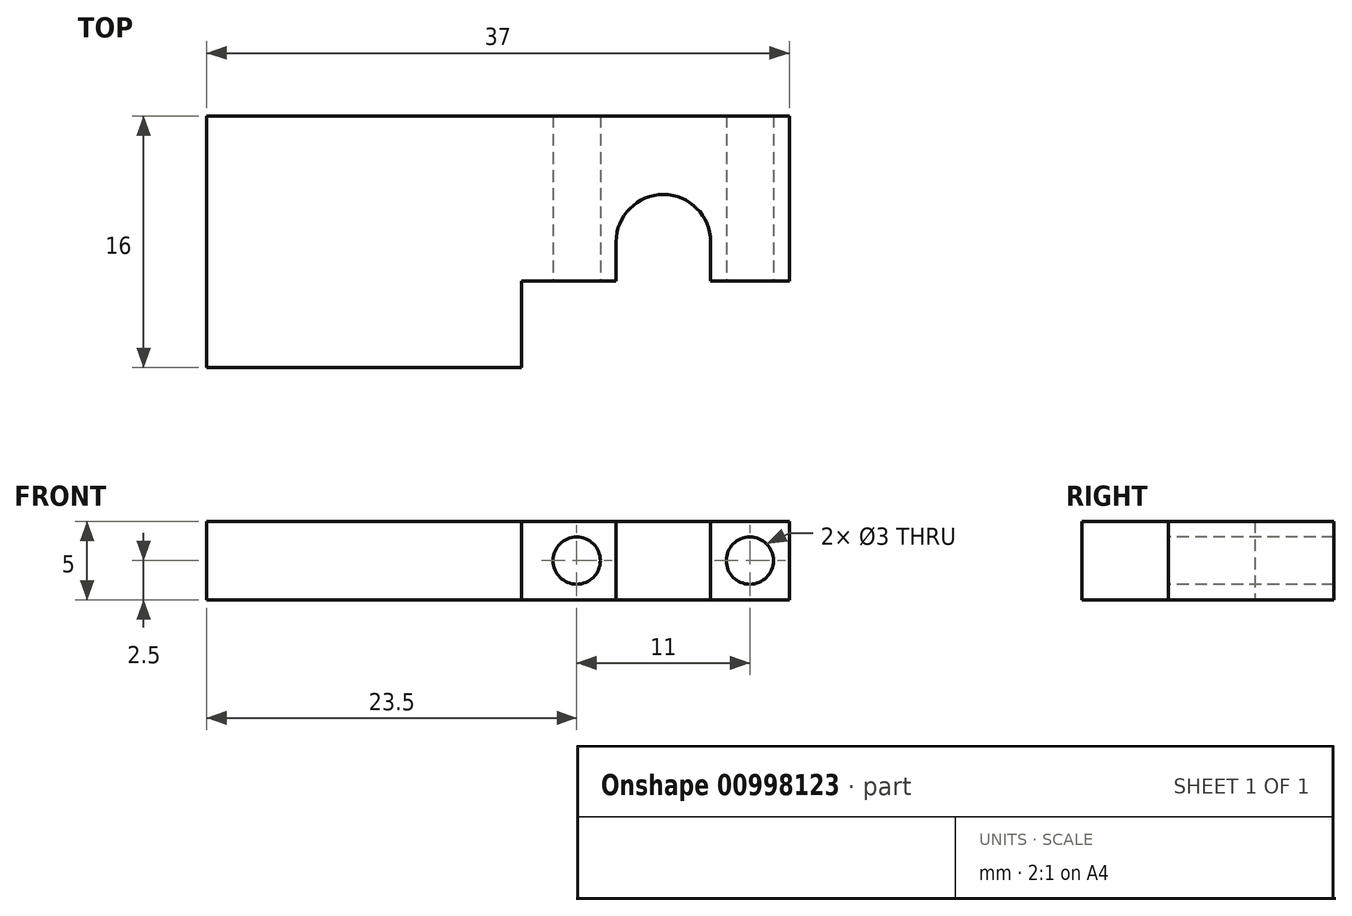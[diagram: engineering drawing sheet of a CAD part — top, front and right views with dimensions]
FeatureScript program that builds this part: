
annotation { "Feature Type Name" : "Feature", "Feature Type Description" : "" }
export const myFeature = defineFeature(function(context is Context, id is Id, definition is map)
    precondition{}
    {
        {
            var Q0;
            Q0=qCreatedBy(makeId("Top.planeOp"),FACE);
            var sketch = newSketch(context, id + "F0", { "sketchPlane" : qUnion([Q0])});
            skLineSegment(sketch, "E0", {"start": v(0, 0) * mm, "end": v(20, 0) * mm});
            skArc(sketch, "E1", {"start": v(32, 8) * mm, "mid": v(29, 11) * mm, "end": v(26, 8) * mm});
            skLineSegment(sketch, "E2", {"start": v(37, 16) * mm, "end": v(0, 16) * mm});
            skLineSegment(sketch, "E3", {"start": v(0, 16) * mm, "end": v(0, 0) * mm});
            skLineSegment(sketch, "E4", {"start": v(20, 0) * mm, "end": v(20, 5.5) * mm});
            skLineSegment(sketch, "E5", {"start": v(20, 5.5) * mm, "end": v(26, 5.5) * mm});
            skLineSegment(sketch, "E6", {"start": v(26, 5.5) * mm, "end": v(26, 8) * mm});
            skLineSegment(sketch, "E7", {"start": v(37, 5.5) * mm, "end": v(37, 16) * mm});
            skLineSegment(sketch, "E8", {"start": v(32, 8) * mm, "end": v(32, 5.5) * mm});
            skLineSegment(sketch, "E9", {"start": v(32, 5.5) * mm, "end": v(37, 5.5) * mm});
            skLineSegment(sketch, "E10", {"start": v(26, 8) * mm, "end": v(32, 8) * mm, "construction": true});
            skLineSegment(sketch, "E11", {"start": v(26, 5.5) * mm, "end": v(32, 5.5) * mm, "construction": true});
            skSolve(sketch);
        }
        {
            var Q0;
            Q0=makeQuery(id+"F0.imprint","IMPRINT",FACE,{"disambiguationData":[TD([[makeQuery(id+"F0.imprint","IMPRINT",EDGE,{"derivedFrom":sQuery(id+"F0.wireOp",EDGE,"E0")}),1.0]])]});
            extrude(context, id + "F1", {"entities" : qUnion([Q0]), "depth" : 5 * mm, "offsetDistance" : 25 * mm});
        }
        {
            var Q0;
            Q0=makeQuery(id+"F1.opExtrude","SWEPT_FACE",FACE,{"disambiguationData":[OSD([sQuery(id+"F0.wireOp",EDGE,"E5")])]});
            var sketch = newSketch(context, id + "F2", { "sketchPlane" : qUnion([Q0])});
            skCircle(sketch, "E12", {"center": v(23.5, 2.5) * mm, "radius": 1.5 * mm});
            skCircle(sketch, "E13", {"center": v(34.5, 2.5) * mm, "radius": 1.5 * mm});
            skLineSegment(sketch, "E14", {"start": v(20, 2.5) * mm, "end": v(37, 2.5) * mm, "construction": true});
            skSolve(sketch);
        }
        {
            var Q0;
            Q0 = qSketchRegion(id + "F2", true);
            extrude(context, id + "F3", {"entities" : qUnion([Q0]), "operationType" : NewBodyOperationType.REMOVE, "endBound" : BoundingType.THROUGH_ALL, "oppositeDirection" : true, "depth" : 25 * mm, "offsetDistance" : 25 * mm});
        }
    });
